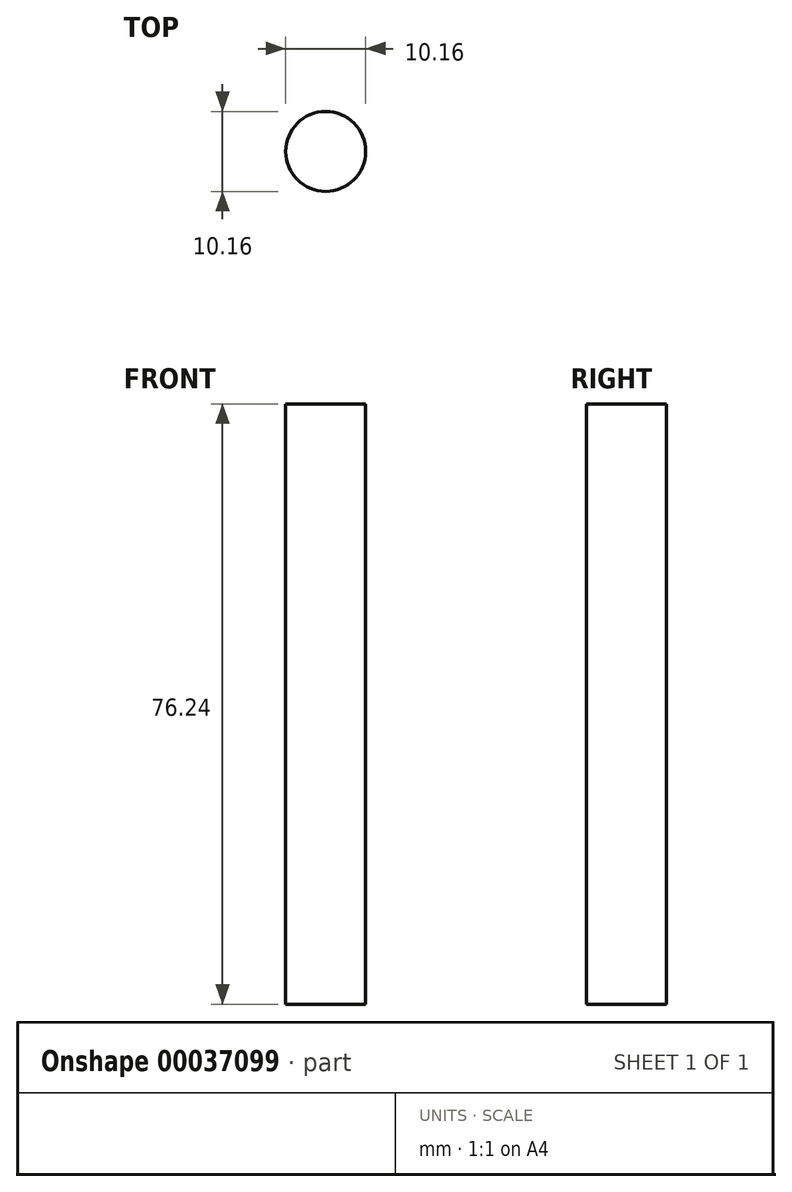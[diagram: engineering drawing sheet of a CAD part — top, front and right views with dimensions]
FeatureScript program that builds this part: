
annotation { "Feature Type Name" : "Feature", "Feature Type Description" : "" }
export const myFeature = defineFeature(function(context is Context, id is Id, definition is map)
    precondition{}
    {
        {
            var Q0;
            Q0=qCreatedBy(makeId("Front.planeOp"),FACE);
            var sketch = newSketch(context, id + "F0", { "sketchPlane" : qUnion([Q0])});
            skLineSegment(sketch, "E0", {"start": v(0.9, -70.43) * mm, "end": v(0.9, 5.77) * mm, "construction": true});
            skLineSegment(sketch, "E1.bottom", {"start": v(0.9, 5.77) * mm, "end": v(5.97, 5.77) * mm});
            skLineSegment(sketch, "E1.top", {"start": v(0.9, -70.47) * mm, "end": v(5.97, -70.47) * mm});
            skLineSegment(sketch, "E1.left", {"start": v(0.9, 5.77) * mm, "end": v(0.9, -70.47) * mm});
            skLineSegment(sketch, "E1.right", {"start": v(5.97, 5.77) * mm, "end": v(5.97, -70.47) * mm});
            skLineSegment(sketch, "E2", {"start": v(0.9, 5.77) * mm, "end": v(0.9, -70.43) * mm});
            skSolve(sketch);
        }
        {
            var Q0;
            Q0 = qSketchRegion(id + "F0", true);
            var Q1;
            Q1=sQuery(id+"F0.wireOp",EDGE,"E2");
            revolve(context, id + "F1", {"entities" : qUnion([Q0]), "axis" : qUnion([Q1]), "revolveType" : RevolveType.FULL});
        }
    });
